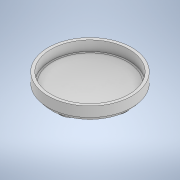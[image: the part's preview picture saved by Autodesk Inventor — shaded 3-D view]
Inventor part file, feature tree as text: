
AUTODESK INVENTOR PART (.ipt)
format: ipt  version: 2022 (Build 260153000, 153)  size: 184,832 bytes
history: native  units: mm
features: sketch x4, revolve x3, pattern_circular x1, extrude x1
ambient origin geometry x8: Origin, YZ Plane, XZ Plane, XY Plane, X Axis, Y Axis, Z Axis, Center Point
bodies: Body1 (feature_tree)
feature tree (9):
  revolve  "Revolution1"  [1 undecoded]
  revolve  "Revolution2"  [1 undecoded]
  revolve  "Revolution4"  Angle=360.0deg
  pattern_circular  "Circular Pattern2"  Count=4 Angle=360.0deg
  extrude  "Extrusion3"  Depth=5.0mm TaperAngle=0.0deg
  sketch  "Sketch2"  dims[d3=50.0mm d4=48.0mm]
  sketch  "Sketch3"  dims[d5=90.0deg d6=10.0mm]
  sketch  "Sketch4"  dims[d7=51.75mm d8=360.0deg]
  sketch  "Sketch6"  dims[d18=13.962634mm d19=40.0mm d20=360.0deg d22=5.0mm d23=0.0mm]
note: 2 required parameter values undecoded (feature->parameter linkage not recoverable at this tier; creation-order binding heuristic only, values carry confidence <= 0.55)
